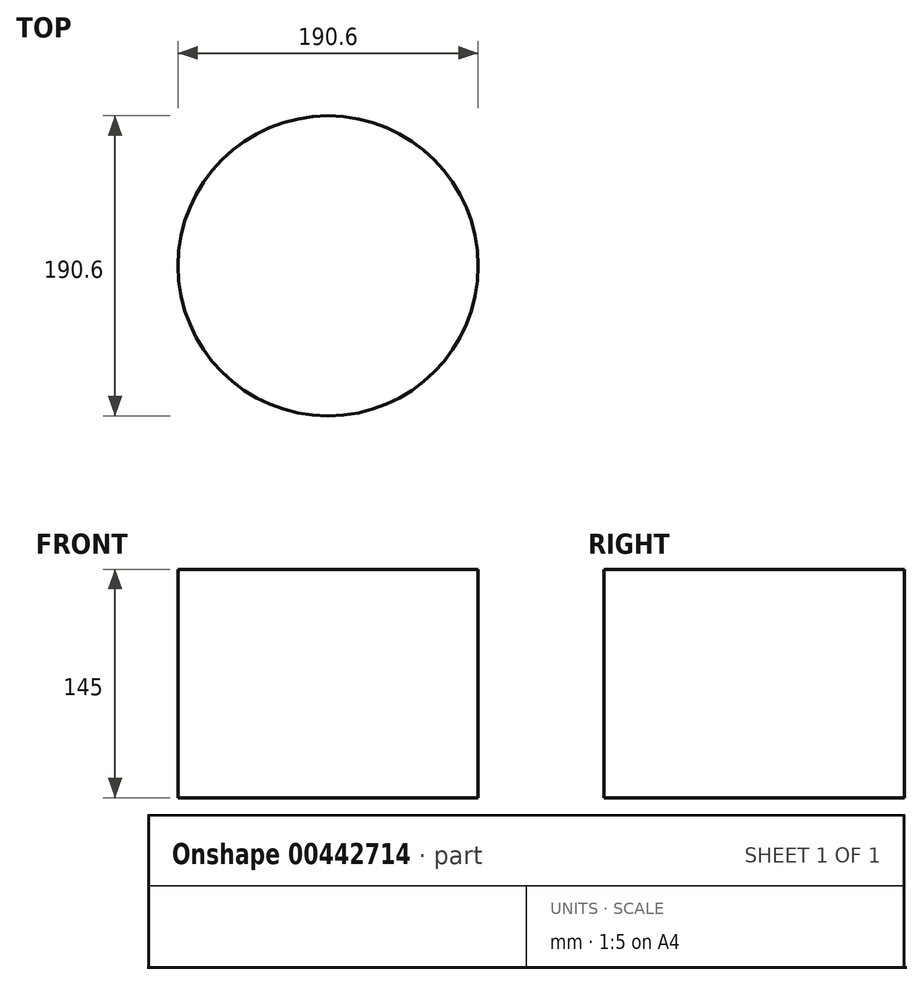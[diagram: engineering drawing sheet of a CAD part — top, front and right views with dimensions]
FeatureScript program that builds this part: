
annotation { "Feature Type Name" : "Feature", "Feature Type Description" : "" }
export const myFeature = defineFeature(function(context is Context, id is Id, definition is map)
    precondition{}
    {
        {
            var Q0;
            Q0=qCreatedBy(makeId("Top.planeOp"),FACE);
            var sketch = newSketch(context, id + "F0", { "sketchPlane" : qUnion([Q0])});
            skCircle(sketch, "E0", {"center": v(0, 0) * mm, "radius": 95.3 * mm});
            skSolve(sketch);
        }
        {
            var Q0;
            Q0 = qSketchRegion(id + "F0", true);
            extrude(context, id + "F1", {"entities" : qUnion([Q0]), "depth" : 145 * mm});
        }
    });
